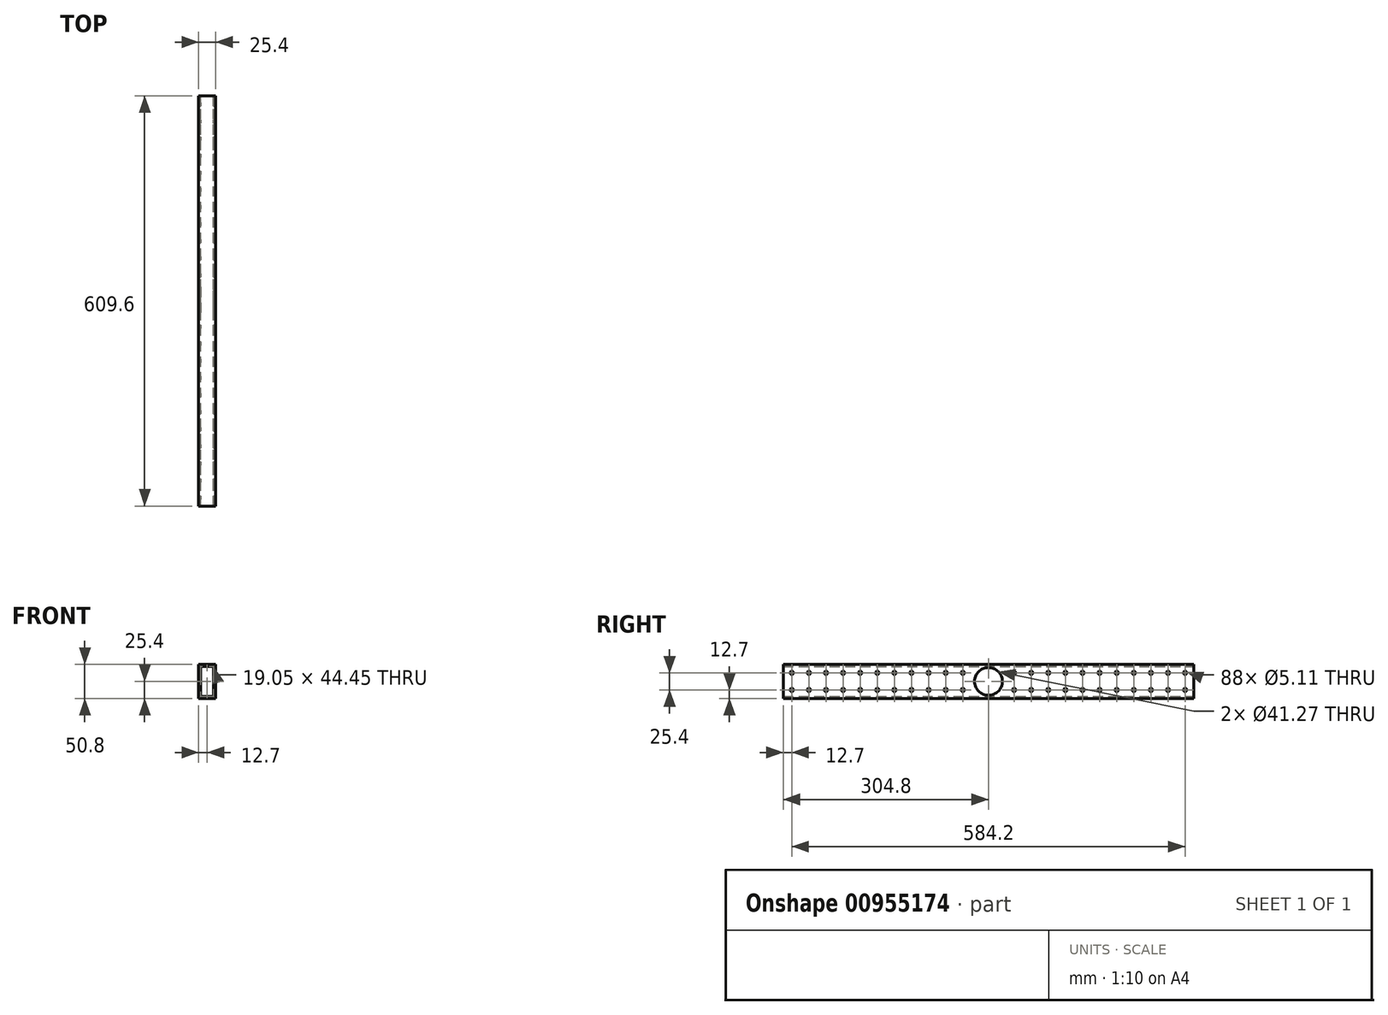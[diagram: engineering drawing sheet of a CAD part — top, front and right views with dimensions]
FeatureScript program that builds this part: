
annotation { "Feature Type Name" : "Feature", "Feature Type Description" : "" }
export const myFeature = defineFeature(function(context is Context, id is Id, definition is map)
    precondition{}
    {
        {
            var Q0;
            Q0=qCreatedBy(makeId("Front.planeOp"),FACE);
            var sketch = newSketch(context, id + "F0", { "sketchPlane" : qUnion([Q0])});
            skLineSegment(sketch, "E0.bottom", {"start": v(-12.7, 25.4) * mm, "end": v(12.7, 25.4) * mm});
            skLineSegment(sketch, "E0.top", {"start": v(-12.7, -25.4) * mm, "end": v(12.7, -25.4) * mm});
            skLineSegment(sketch, "E0.left", {"start": v(-12.7, 25.4) * mm, "end": v(-12.7, -25.4) * mm});
            skLineSegment(sketch, "E0.right", {"start": v(12.7, 25.4) * mm, "end": v(12.7, -25.4) * mm});
            skPoint(sketch, "E0.middle", {"position": v(0, 0) * mm});
            skLineSegment(sketch, "E1.0", {"start": v(-9.52, 22.22) * mm, "end": v(9.53, 22.22) * mm});
            skLineSegment(sketch, "E1.1", {"start": v(-9.52, 22.22) * mm, "end": v(-9.53, -22.23) * mm});
            skLineSegment(sketch, "E1.2", {"start": v(-9.53, -22.23) * mm, "end": v(9.53, -22.23) * mm});
            skLineSegment(sketch, "E1.3", {"start": v(9.53, 22.22) * mm, "end": v(9.53, -22.23) * mm});
            skSolve(sketch);
        }
        {
            var Q0;
            Q0=qSketchRegion(id+"F0",true);
            extrude(context, id + "F1", {"entities" : qUnion([Q0]), "depth" : 609.6 * mm, "offsetDistance" : 25.4 * mm});
        }
        {
            var Q0;
            Q0=makeQuery(id+"F1.opExtrude","SWEPT_FACE",FACE,{"disambiguationData":[OSD([sQuery(id+"F0.wireOp",EDGE,"E0.right")])]});
            var sketch = newSketch(context, id + "F2", { "sketchPlane" : qUnion([Q0])});
            skCircle(sketch, "E2", {"center": v(-596.9, 12.7) * mm, "radius": 2.55 * mm});
            skCircle(sketch, "E3.0.1.0", {"center": v(-596.9, -12.7) * mm, "radius": 2.55 * mm});
            skCircle(sketch, "E3.1.0.0", {"center": v(-571.5, 12.7) * mm, "radius": 2.55 * mm});
            skCircle(sketch, "E3.1.1.0", {"center": v(-571.5, -12.7) * mm, "radius": 2.55 * mm});
            skCircle(sketch, "E3.2.0.0", {"center": v(-546.1, 12.7) * mm, "radius": 2.55 * mm});
            skCircle(sketch, "E3.2.1.0", {"center": v(-546.1, -12.7) * mm, "radius": 2.55 * mm});
            skCircle(sketch, "E3.3.0.0", {"center": v(-520.7, 12.7) * mm, "radius": 2.55 * mm});
            skCircle(sketch, "E3.3.1.0", {"center": v(-520.7, -12.7) * mm, "radius": 2.55 * mm});
            skCircle(sketch, "E3.4.0.0", {"center": v(-495.3, 12.7) * mm, "radius": 2.55 * mm});
            skCircle(sketch, "E3.4.1.0", {"center": v(-495.3, -12.7) * mm, "radius": 2.55 * mm});
            skCircle(sketch, "E3.5.0.0", {"center": v(-469.9, 12.7) * mm, "radius": 2.55 * mm});
            skCircle(sketch, "E3.5.1.0", {"center": v(-469.9, -12.7) * mm, "radius": 2.55 * mm});
            skCircle(sketch, "E3.6.0.0", {"center": v(-444.5, 12.7) * mm, "radius": 2.55 * mm});
            skCircle(sketch, "E3.6.1.0", {"center": v(-444.5, -12.7) * mm, "radius": 2.55 * mm});
            skCircle(sketch, "E3.7.0.0", {"center": v(-419.1, 12.7) * mm, "radius": 2.55 * mm});
            skCircle(sketch, "E3.7.1.0", {"center": v(-419.1, -12.7) * mm, "radius": 2.55 * mm});
            skCircle(sketch, "E3.8.0.0", {"center": v(-393.7, 12.7) * mm, "radius": 2.55 * mm});
            skCircle(sketch, "E3.8.1.0", {"center": v(-393.7, -12.7) * mm, "radius": 2.55 * mm});
            skCircle(sketch, "E3.9.0.0", {"center": v(-368.3, 12.7) * mm, "radius": 2.55 * mm});
            skCircle(sketch, "E3.9.1.0", {"center": v(-368.3, -12.7) * mm, "radius": 2.55 * mm});
            skCircle(sketch, "E3.10.0.0", {"center": v(-342.9, 12.7) * mm, "radius": 2.55 * mm});
            skCircle(sketch, "E3.10.1.0", {"center": v(-342.9, -12.7) * mm, "radius": 2.55 * mm});
            skCircle(sketch, "E3.11.0.0", {"center": v(-317.5, 12.7) * mm, "radius": 2.55 * mm});
            skCircle(sketch, "E3.11.1.0", {"center": v(-317.5, -12.7) * mm, "radius": 2.55 * mm});
            skCircle(sketch, "E3.12.0.0", {"center": v(-292.1, 12.7) * mm, "radius": 2.55 * mm});
            skCircle(sketch, "E3.12.1.0", {"center": v(-292.1, -12.7) * mm, "radius": 2.55 * mm});
            skCircle(sketch, "E3.13.0.0", {"center": v(-266.7, 12.7) * mm, "radius": 2.55 * mm});
            skCircle(sketch, "E3.13.1.0", {"center": v(-266.7, -12.7) * mm, "radius": 2.55 * mm});
            skCircle(sketch, "E3.14.0.0", {"center": v(-241.3, 12.7) * mm, "radius": 2.55 * mm});
            skCircle(sketch, "E3.14.1.0", {"center": v(-241.3, -12.7) * mm, "radius": 2.55 * mm});
            skCircle(sketch, "E3.15.0.0", {"center": v(-215.9, 12.7) * mm, "radius": 2.55 * mm});
            skCircle(sketch, "E3.15.1.0", {"center": v(-215.9, -12.7) * mm, "radius": 2.55 * mm});
            skCircle(sketch, "E3.16.0.0", {"center": v(-190.5, 12.7) * mm, "radius": 2.55 * mm});
            skCircle(sketch, "E3.16.1.0", {"center": v(-190.5, -12.7) * mm, "radius": 2.55 * mm});
            skCircle(sketch, "E3.17.0.0", {"center": v(-165.1, 12.7) * mm, "radius": 2.55 * mm});
            skCircle(sketch, "E3.17.1.0", {"center": v(-165.1, -12.7) * mm, "radius": 2.55 * mm});
            skCircle(sketch, "E3.18.0.0", {"center": v(-139.7, 12.7) * mm, "radius": 2.55 * mm});
            skCircle(sketch, "E3.18.1.0", {"center": v(-139.7, -12.7) * mm, "radius": 2.55 * mm});
            skCircle(sketch, "E3.19.0.0", {"center": v(-114.3, 12.7) * mm, "radius": 2.55 * mm});
            skCircle(sketch, "E3.19.1.0", {"center": v(-114.3, -12.7) * mm, "radius": 2.55 * mm});
            skCircle(sketch, "E3.20.0.0", {"center": v(-88.9, 12.7) * mm, "radius": 2.55 * mm});
            skCircle(sketch, "E3.20.1.0", {"center": v(-88.9, -12.7) * mm, "radius": 2.55 * mm});
            skCircle(sketch, "E3.21.0.0", {"center": v(-63.5, 12.7) * mm, "radius": 2.55 * mm});
            skCircle(sketch, "E3.21.1.0", {"center": v(-63.5, -12.7) * mm, "radius": 2.55 * mm});
            skCircle(sketch, "E3.22.0.0", {"center": v(-38.1, 12.7) * mm, "radius": 2.55 * mm});
            skCircle(sketch, "E3.22.1.0", {"center": v(-38.1, -12.7) * mm, "radius": 2.55 * mm});
            skCircle(sketch, "E3.23.0.0", {"center": v(-12.7, 12.7) * mm, "radius": 2.55 * mm});
            skCircle(sketch, "E3.23.1.0", {"center": v(-12.7, -12.7) * mm, "radius": 2.55 * mm});
            skLineSegment(sketch, "E3.direction1", {"start": v(-596.9, 12.7) * mm, "end": v(-571.5, 12.7) * mm, "construction": true});
            skLineSegment(sketch, "E3.direction2", {"start": v(-596.9, 12.7) * mm, "end": v(-596.9, -12.7) * mm, "construction": true});
            skSolve(sketch);
        }
        {
            var Q0;
            Q0=qSketchRegion(id+"F2",true);
            extrude(context, id + "F3", {"entities" : qUnion([Q0]), "operationType" : NewBodyOperationType.REMOVE, "oppositeDirection" : true, "depth" : 25.4 * mm, "offsetDistance" : 25.4 * mm});
        }
        {
            var Q0;
            Q0=makeQuery(id+"F1.opExtrude","SWEPT_FACE",FACE,{"disambiguationData":[OSD([sQuery(id+"F0.wireOp",EDGE,"E0.right")])]});
            var sketch = newSketch(context, id + "F4", { "sketchPlane" : qUnion([Q0])});
            skCircle(sketch, "E4", {"center": v(-304.8, 0) * mm, "radius": 20.64 * mm});
            skPoint(sketch, "E4.centerSnap0", {"position": v(-304.8, 25.4) * mm});
            skSolve(sketch);
        }
        {
            var Q0;
            Q0=qSketchRegion(id+"F4",true);
            extrude(context, id + "F5", {"entities" : qUnion([Q0]), "operationType" : NewBodyOperationType.REMOVE, "oppositeDirection" : true, "depth" : 25.4 * mm, "offsetDistance" : 25.4 * mm});
        }
    });
